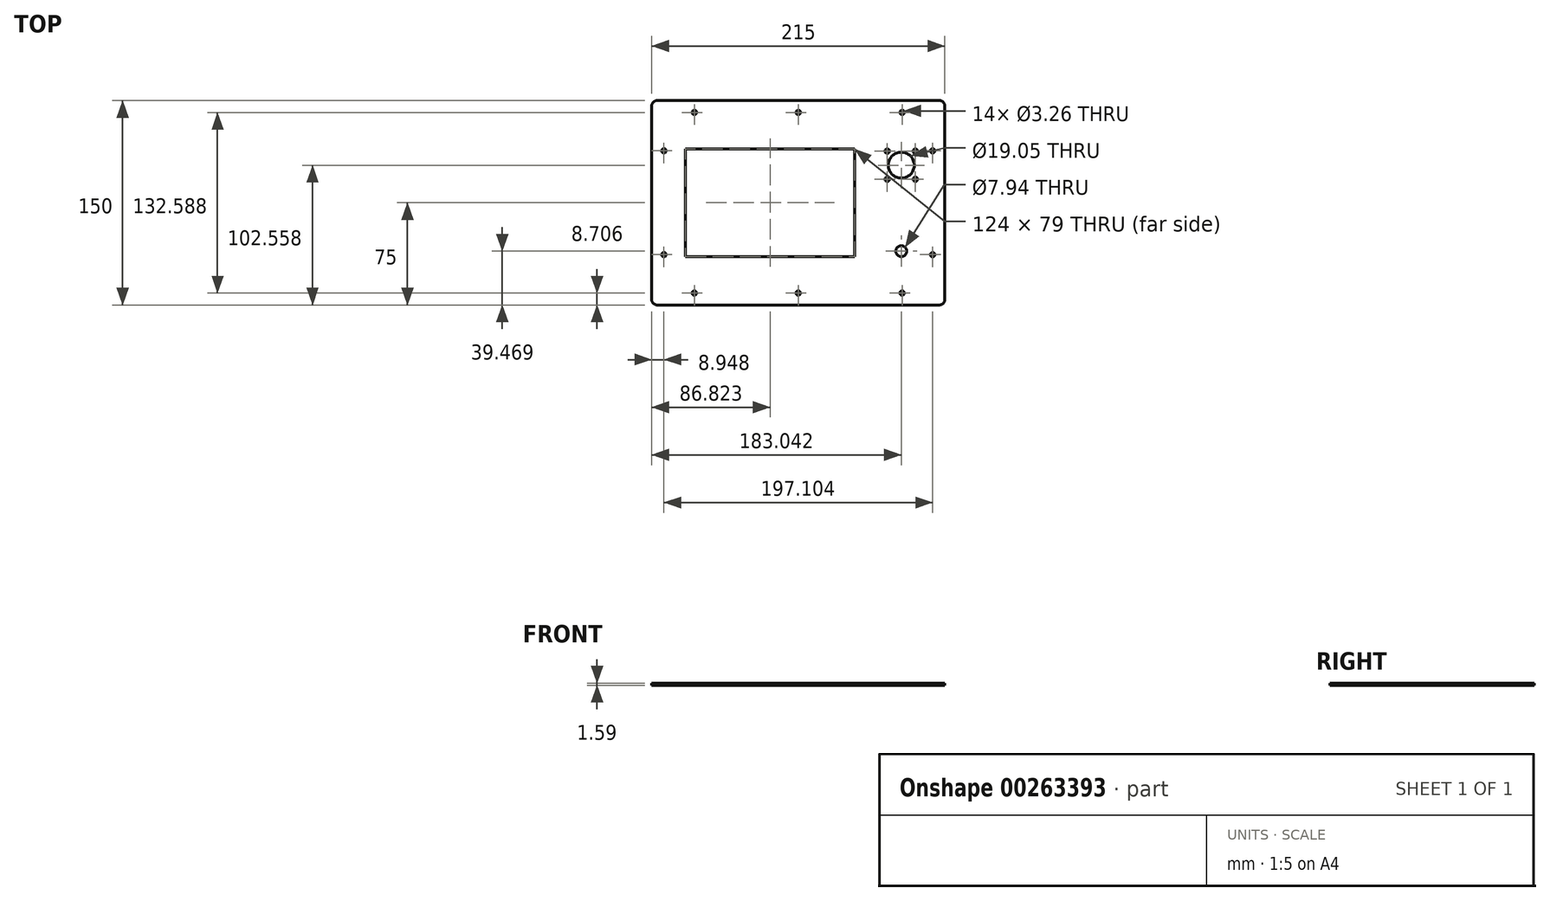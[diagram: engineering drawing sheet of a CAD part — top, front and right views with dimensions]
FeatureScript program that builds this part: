
annotation { "Feature Type Name" : "Feature", "Feature Type Description" : "" }
export const myFeature = defineFeature(function(context is Context, id is Id, definition is map)
    precondition{}
    {
        {
            var Q0;
            Q0=qCreatedBy(makeId("Top.planeOp"),FACE);
            var sketch = newSketch(context, id + "F0", { "sketchPlane" : qUnion([Q0])});
            skLineSegment(sketch, "E0.bottom", {"start": v(107.5, -75) * mm, "end": v(-107.5, -75) * mm});
            skLineSegment(sketch, "E0.top", {"start": v(107.5, 75) * mm, "end": v(-107.5, 75) * mm});
            skLineSegment(sketch, "E0.left", {"start": v(107.5, -75) * mm, "end": v(107.5, 75) * mm});
            skLineSegment(sketch, "E0.right", {"start": v(-107.5, -75) * mm, "end": v(-107.5, 75) * mm});
            skPoint(sketch, "E0.middle", {"position": v(0, 0) * mm});
            skLineSegment(sketch, "E1.bottom", {"start": v(41.32, -39.5) * mm, "end": v(-82.68, -39.5) * mm});
            skLineSegment(sketch, "E1.top", {"start": v(41.32, 39.5) * mm, "end": v(-82.68, 39.5) * mm});
            skLineSegment(sketch, "E1.left", {"start": v(41.32, -39.5) * mm, "end": v(41.32, 39.5) * mm});
            skLineSegment(sketch, "E1.right", {"start": v(-82.68, -39.5) * mm, "end": v(-82.68, 39.5) * mm});
            skPoint(sketch, "E1.middle", {"position": v(-20.68, 0) * mm});
            skCircle(sketch, "E2", {"center": v(75.54, 27.56) * mm, "radius": 9.53 * mm});
            skLineSegment(sketch, "E3.bottom", {"start": v(85.85, 17.25) * mm, "end": v(65.23, 17.25) * mm, "construction": true});
            skLineSegment(sketch, "E3.top", {"start": v(85.85, 37.87) * mm, "end": v(65.23, 37.87) * mm, "construction": true});
            skLineSegment(sketch, "E3.left", {"start": v(85.85, 17.25) * mm, "end": v(85.85, 37.87) * mm, "construction": true});
            skLineSegment(sketch, "E3.right", {"start": v(65.23, 17.25) * mm, "end": v(65.23, 37.87) * mm, "construction": true});
            skCircle(sketch, "E4", {"center": v(85.85, 37.87) * mm, "radius": 1.63 * mm});
            skLineSegment(sketch, "E5.bottom", {"start": v(98.55, -66.3) * mm, "end": v(-98.55, -66.3) * mm, "construction": true});
            skLineSegment(sketch, "E5.top", {"start": v(98.55, 66.3) * mm, "end": v(-98.55, 66.3) * mm, "construction": true});
            skLineSegment(sketch, "E5.left", {"start": v(98.55, -66.3) * mm, "end": v(98.55, 66.3) * mm, "construction": true});
            skLineSegment(sketch, "E5.right", {"start": v(-98.55, -66.3) * mm, "end": v(-98.55, 66.3) * mm, "construction": true});
            skCircle(sketch, "E6", {"center": v(-98.55, 38.1) * mm, "radius": 1.63 * mm});
            skCircle(sketch, "E7", {"center": v(0, 66.3) * mm, "radius": 1.63 * mm});
            skCircle(sketch, "E8", {"center": v(-76.2, 66.3) * mm, "radius": 1.63 * mm});
            skCircle(sketch, "E9.MirrorC", {"center": v(76.2, 66.3) * mm, "radius": 1.63 * mm});
            skCircle(sketch, "E10.MirrorC", {"center": v(98.55, 38.1) * mm, "radius": 1.63 * mm});
            skCircle(sketch, "E11.MirrorC", {"center": v(-98.55, -38.1) * mm, "radius": 1.63 * mm});
            skCircle(sketch, "E12.MirrorC", {"center": v(-76.2, -66.3) * mm, "radius": 1.63 * mm});
            skCircle(sketch, "E13.MirrorC", {"center": v(0, -66.3) * mm, "radius": 1.63 * mm});
            skCircle(sketch, "E14.MirrorC", {"center": v(76.2, -66.3) * mm, "radius": 1.63 * mm});
            skCircle(sketch, "E15.MirrorC", {"center": v(98.55, -38.1) * mm, "radius": 1.63 * mm});
            skCircle(sketch, "E16", {"center": v(65.23, 37.87) * mm, "radius": 1.63 * mm});
            skCircle(sketch, "E17", {"center": v(65.23, 17.25) * mm, "radius": 1.63 * mm});
            skCircle(sketch, "E18", {"center": v(85.85, 17.25) * mm, "radius": 1.63 * mm});
            skCircle(sketch, "E19", {"center": v(75.54, -35.53) * mm, "radius": 3.97 * mm});
            skLineSegment(sketch, "E20", {"start": v(75.54, 27.56) * mm, "end": v(75.54, -35.53) * mm, "construction": true});
            skLineSegment(sketch, "E21", {"start": v(41.32, 39.5) * mm, "end": v(65.23, 39.5) * mm, "construction": true});
            skLineSegment(sketch, "E22", {"start": v(41.32, -39.5) * mm, "end": v(75.54, -39.5) * mm, "construction": true});
            skSolve(sketch);
        }
        {
            var Q0;
            Q0 = qSketchRegion(id + "F0", true);
            extrude(context, id + "F1", {"entities" : qUnion([Q0]), "depth" : 1.59 * mm});
        }
        {
            var Q0;
            Q0=makeQuery(id+"F1.opExtrude","SWEPT_EDGE",EDGE,{"disambiguationData":[OSD([sQuery(id+"F0.wireOp",EDGE,"E0.top"),sQuery(id+"F0.wireOp",EDGE,"E0.right")])]});
            var Q1;
            Q1=makeQuery(id+"F1.opExtrude","SWEPT_EDGE",EDGE,{"disambiguationData":[OSD([sQuery(id+"F0.wireOp",EDGE,"E0.bottom"),sQuery(id+"F0.wireOp",EDGE,"E0.right")])]});
            var Q2;
            Q2=makeQuery(id+"F1.opExtrude","SWEPT_EDGE",EDGE,{"disambiguationData":[OSD([sQuery(id+"F0.wireOp",EDGE,"E0.bottom"),sQuery(id+"F0.wireOp",EDGE,"E0.left")])]});
            var Q3;
            Q3=makeQuery(id+"F1.opExtrude","SWEPT_EDGE",EDGE,{"disambiguationData":[OSD([sQuery(id+"F0.wireOp",EDGE,"E0.top"),sQuery(id+"F0.wireOp",EDGE,"E0.left")])]});
            fillet(context, id + "F2", {"entities" : qUnion([Q0, Q1, Q2, Q3]), "radius" : 4 * mm, "tangentPropagation" : true, "allowEdgeOverflow" : false});
        }
    });
